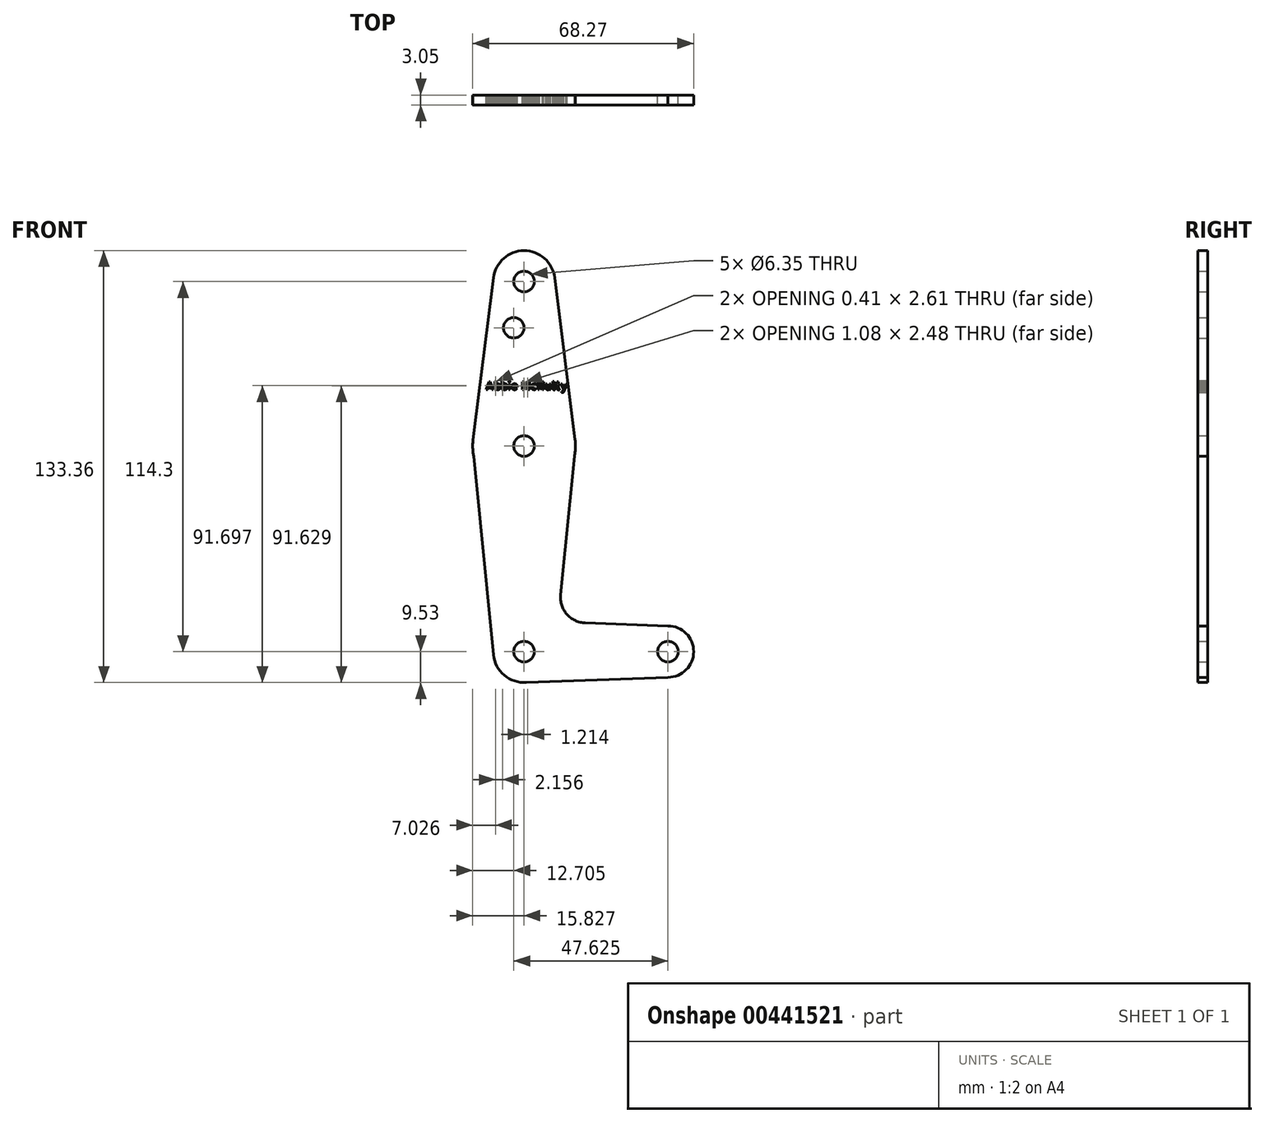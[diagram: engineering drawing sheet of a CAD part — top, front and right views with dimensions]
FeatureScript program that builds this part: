
annotation { "Feature Type Name" : "Feature", "Feature Type Description" : "" }
export const myFeature = defineFeature(function(context is Context, id is Id, definition is map)
    precondition{}
    {
        {
            var Q0;
            Q0=qCreatedBy(makeId("Front.planeOp"),FACE);
            var sketch = newSketch(context, id + "F0", { "sketchPlane" : qUnion([Q0])});
            skCircle(sketch, "E0", {"center": v(0, 114.3) * mm, "radius": 9.53 * mm});
            skCircle(sketch, "E1", {"center": v(0, 63.5) * mm, "radius": 15.88 * mm});
            skCircle(sketch, "E2", {"center": v(0, 0) * mm, "radius": 9.53 * mm});
            skLineSegment(sketch, "E3", {"start": v(0, 0) * mm, "end": v(44.45, 0) * mm, "construction": true});
            skCircle(sketch, "E4", {"center": v(44.45, 0) * mm, "radius": 7.94 * mm});
            skLineSegment(sketch, "E5", {"start": v(0, 63.5) * mm, "end": v(0, 0) * mm, "construction": true});
            skLineSegment(sketch, "E6", {"start": v(-15.88, 63.5) * mm, "end": v(-9.48, -0.94) * mm});
            skLineSegment(sketch, "E7", {"start": v(11.28, 17.59) * mm, "end": v(15.87, 63.5) * mm});
            skLineSegment(sketch, "E8", {"start": v(0, 114.3) * mm, "end": v(0, 63.5) * mm, "construction": true});
            skCircle(sketch, "E9", {"center": v(0, 114.3) * mm, "radius": 3.18 * mm});
            skCircle(sketch, "E10", {"center": v(0, 63.5) * mm, "radius": 3.18 * mm});
            skCircle(sketch, "E11", {"center": v(0, 0) * mm, "radius": 3.18 * mm});
            skCircle(sketch, "E12", {"center": v(44.45, 0) * mm, "radius": 3.18 * mm});
            skCircle(sketch, "E13", {"center": v(-3.18, 100.03) * mm, "radius": 3.18 * mm});
            skLineSegment(sketch, "E14", {"start": v(18.91, 8.85) * mm, "end": v(44.45, 7.94) * mm});
            skLineSegment(sketch, "E15", {"start": v(0, -9.52) * mm, "end": v(44.45, -7.94) * mm});
            skArc(sketch, "E16.filletArc", {"start": v(11.28, 17.59) * mm, "mid": v(13.2, 11.57) * mm, "end": v(18.91, 8.85) * mm});
            skLineSegment(sketch, "E17", {"start": v(9.45, 115.5) * mm, "end": v(16, 63.5) * mm});
            skLineSegment(sketch, "E18", {"start": v(-9.14, 117.92) * mm, "end": v(-16, 63.5) * mm});
            skText(sketch, "E19", { "text": "Abbie McNulty", "fontName": "AllertaStencil-Regular.ttf"});
            const initialGuessF0  = {"E19": [-0.0119, 0.08086, 1, 0, 0.00248]};
            skSetInitialGuess(sketch, initialGuessF0);
            skSolve(sketch);
        }
        {
            var Q0;
            Q0 = qSketchRegion(id + "F0", true);
            extrude(context, id + "F1", {"entities" : qUnion([Q0]), "depth" : 3.05 * mm});
        }
    });
